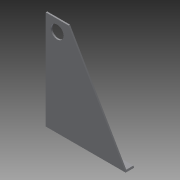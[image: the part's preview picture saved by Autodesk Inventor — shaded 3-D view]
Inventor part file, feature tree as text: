
AUTODESK INVENTOR PART (.ipt)
format: ipt  version: 2013 (Build 170138000, 138)  size: 94,720 bytes
history: native  units: in
note: dims shown in document units (in); Inventor stores cm internally (conversion verified against a paired STEP export)
features: extrude x3, sketch x3
ambient origin geometry x8: Origin, YZ Plane, XZ Plane, XY Plane, X Axis, Y Axis, Z Axis, Center Point
bodies: Solid1 (feature_tree)
feature tree (6):
  extrude  "Extrusion1"  Depth=8.688in
  extrude  "Extrusion2"  Depth=0.125in TaperAngle=0.0deg
  extrude  "Extrusion3"  Depth=0.75in TaperAngle=0.0deg
  sketch  "Sketch1"  dims[d0=2.0in d1=8.688in]
  sketch  "Sketch2"  dims[d2=60.0deg d3=0.125in d4=0.0in]
  sketch  "Sketch3"  dims[d5=0.125in d6=0.75in d7=0.0in d8=1.0in d9=1.0in d10=1.125in d11=1.0in d12=0.0in]
